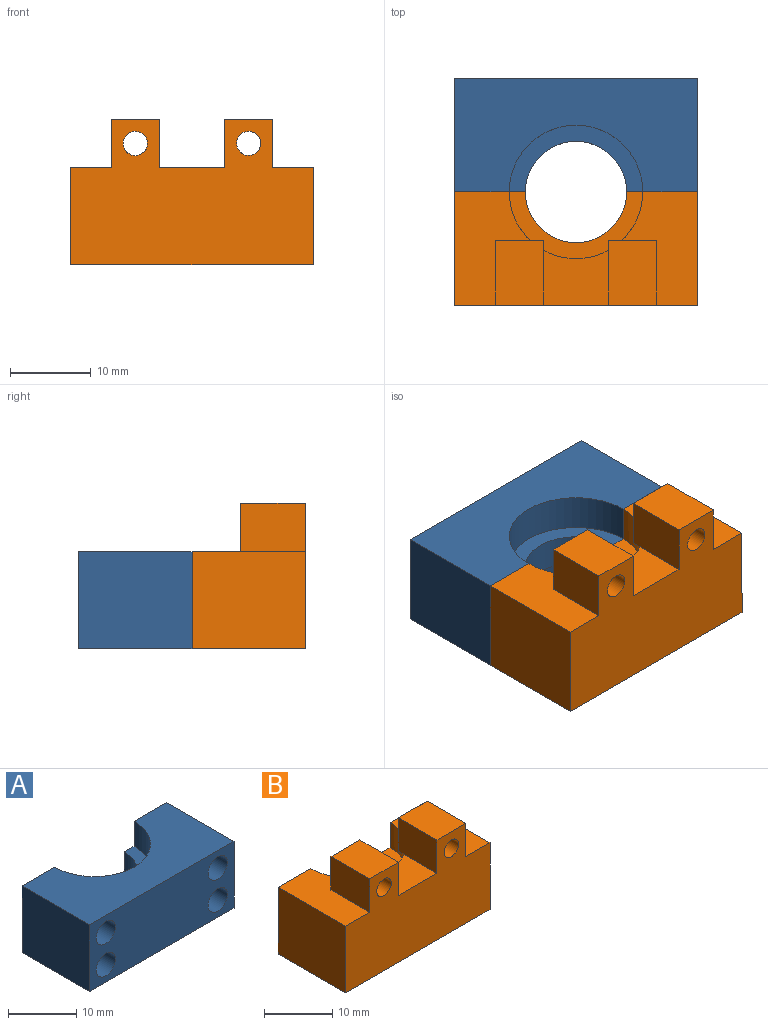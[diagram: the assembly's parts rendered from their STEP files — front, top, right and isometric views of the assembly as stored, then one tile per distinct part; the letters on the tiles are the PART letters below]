
ASSEMBLY  parts=2 mates=1
PART A: 16 faces, bbox 30x14x12 mm
  f0: plane 12x8.75mm, normal (0,1,0), area 63.9mm2, adj f1,f5,f6,f7,f8,f9,f10,f11
  f1: plane 30x14mm, normal (0,0,-1), area 313.1mm2, adj f0,f2,f3,f4,f5,f9
  f2: plane 30x12mm, normal (0,-1,0), area 309.7mm2, adj f1,f3,f5,f6,f12,f13,f14,f15
  f3: plane 14x12mm, normal (1,0,0), area 168mm2, adj f1,f2,f4,f6
  f4: plane 12x8.75mm, normal (0,1,0), area 63.9mm2, adj f1,f3,f6,f7,f8,f9,f10,f11
  f5: plane 14x12mm, normal (-1,0,0), area 168mm2, adj f0,f1,f2,f6
  f6: plane 30x14mm, normal (0,0,1), area 313.1mm2, adj f0,f2,f3,f4,f5,f7
  f7: cylinder r=8.25mm len=16.5mm, axis (0,0,1), area 116.6mm2, adj f0,f4,f6,f8
  f8: plane 16.5x8.25mm, normal (0,0,1), area 45.6mm2, adj f0,f4,f7,f11
  f9: cylinder r=8.25mm len=16.5mm, axis (0,0,-1), area 90.7mm2, adj f0,f1,f4,f10
  f10: plane 16.5x8.25mm, normal (0,0,-1), area 45.6mm2, adj f0,f4,f9,f11
  f11: cylinder r=6.25mm len=12.5mm, axis (0,0,1), area 78.5mm2, adj f0,f4,f8,f10
  f12: cylinder r=2mm len=14mm, axis (0,1,0), area 175.9mm2, adj f2,f4
  f13: cylinder r=2mm len=14mm, axis (0,1,0), area 175.9mm2, adj f2,f4
  f14: cylinder r=2mm len=14mm, axis (0,1,0), area 175.9mm2, adj f0,f2
  f15: cylinder r=2mm len=14mm, axis (0,1,0), area 175.9mm2, adj f0,f2
PART B: 34 faces, bbox 30x14x18 mm
  f0: plane 14x9.34mm, normal (0,0,1), area 85.3mm2, adj f5,f6,f7,f9,f22,f33
  f1: plane 8x6.78mm, normal (0,0,1), area 48.7mm2, adj f5,f9,f23,f26
  f2: plane 14x9.34mm, normal (0,0,1), area 85.3mm2, adj f3,f5,f8,f9,f25,f31
  f3: plane 12x8.75mm, normal (0,1,0), area 63.9mm2, adj f2,f4,f8,f9,f10,f11,f12,f13
  f4: plane 30x14mm, normal (0,0,-1), area 313.1mm2, adj f3,f5,f6,f7,f8,f11
  f5: plane 30x18mm, normal (0,-1,0), area 417.9mm2, adj f0,f1,f2,f4,f6,f8,f22,f23
  f6: plane 14x12mm, normal (1,0,0), area 168mm2, adj f0,f4,f5,f7
  f7: plane 12x8.75mm, normal (0,1,0), area 63.9mm2, adj f0,f4,f6,f9,f10,f11,f12,f13
  f8: plane 14x12mm, normal (-1,0,0), area 168mm2, adj f2,f3,f4,f5
  f9: cylinder r=8.25mm len=16.5mm, axis (0,0,1), area 116.6mm2, adj f0,f1,f2,f3,f7,f10,f30,f32
  f10: plane 16.5x8.25mm, normal (0,0,1), area 45.6mm2, adj f3,f7,f9,f13
  f11: cylinder r=8.25mm len=16.5mm, axis (0,0,-1), area 90.7mm2, adj f3,f4,f7,f12
  f12: plane 16.5x8.25mm, normal (0,0,-1), area 45.6mm2, adj f3,f7,f11,f13
  f13: cylinder r=6.25mm len=12.5mm, axis (0,0,1), area 78.5mm2, adj f3,f7,f10,f12
  f14: cylinder r=2mm len=10mm, axis (0,1,0), area 125.7mm2, adj f7,f15
  f15: plane 4x4mm, normal (0,1,0), area 12.6mm2, adj f14
  f16: cylinder r=2mm len=10mm, axis (0,1,0), area 125.7mm2, adj f7,f17
  f17: plane 4x4mm, normal (0,1,0), area 12.6mm2, adj f16
  f18: cylinder r=2mm len=10mm, axis (0,1,0), area 125.7mm2, adj f3,f19
  f19: plane 4x4mm, normal (0,1,0), area 12.6mm2, adj f18
  f20: cylinder r=2mm len=10mm, axis (0,1,0), area 125.7mm2, adj f3,f21
  f21: plane 4x4mm, normal (0,1,0), area 12.6mm2, adj f20
  f22: plane 8x6mm, normal (1,0,0), area 48mm2, adj f0,f5,f24,f33
  f23: plane 8x6mm, normal (-1,0,0), area 48mm2, adj f1,f5,f24,f32,f33
  f24: plane 8x6mm, normal (0,0,1), area 48mm2, adj f5,f22,f23,f33
  f25: plane 8x6mm, normal (-1,0,0), area 48mm2, adj f2,f5,f27,f31
  f26: plane 8x6mm, normal (1,0,0), area 48mm2, adj f1,f5,f27,f30,f31
  f27: plane 8x6mm, normal (0,0,1), area 48mm2, adj f5,f25,f26,f31
  f28: cylinder r=1.5mm len=8mm, axis (0,1,0), area 75.4mm2, adj f5,f31
  f29: cylinder r=1.5mm len=8mm, axis (0,1,0), area 75.4mm2, adj f5,f33
  f30: plane 1.66x1.22mm, normal (0,0,-1), area 1.1mm2, adj f9,f26,f31
  f31: plane 6x6mm, normal (0,1,0), area 28.9mm2, adj f2,f25,f26,f27,f28,f30
  f32: plane 1.66x1.22mm, normal (0,0,-1), area 1.1mm2, adj f9,f23,f33
  f33: plane 6x6mm, normal (0,1,0), area 28.9mm2, adj f0,f22,f23,f24,f29,f32
PLACE A rot(axis=(0,0,1),180deg) t=(9,-25.22,28.81)mm
PLACE B t=(9,-39.22,28.81)mm
MATE cylindrical A.f14 <-> B.f16  axis (0,-1,0) through (20.62,-32.22,31.96)mm
